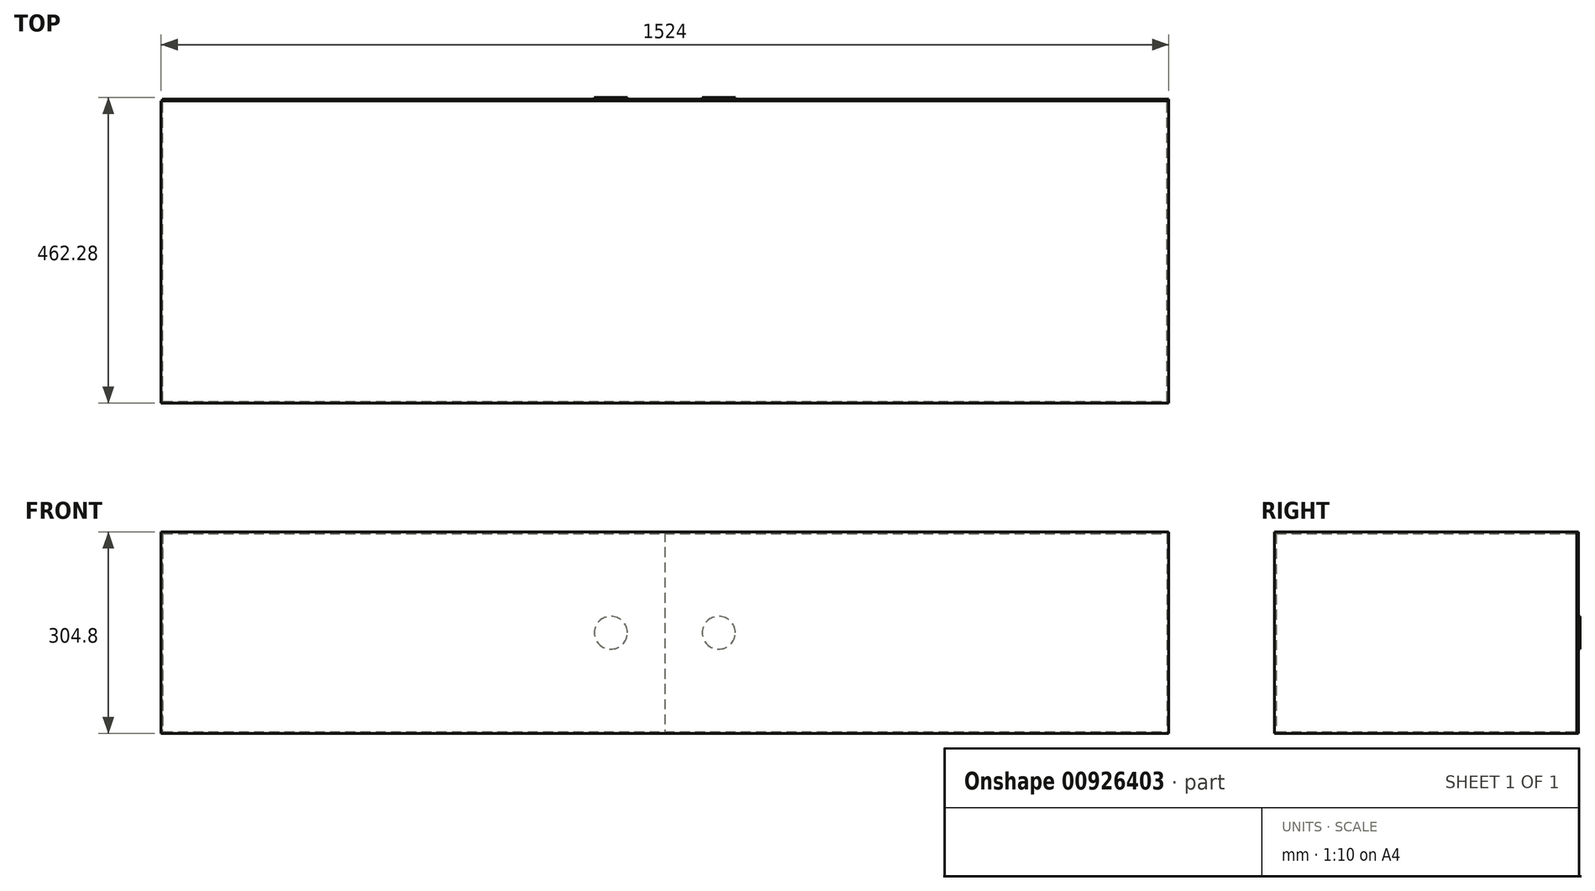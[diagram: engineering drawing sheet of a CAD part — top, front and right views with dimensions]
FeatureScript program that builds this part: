
annotation { "Feature Type Name" : "Feature", "Feature Type Description" : "" }
export const myFeature = defineFeature(function(context is Context, id is Id, definition is map)
    precondition{}
    {
        {
            var Q0;
            Q0=qCreatedBy(makeId("Front.planeOp"),FACE);
            var sketch = newSketch(context, id + "F0", { "sketchPlane" : qUnion([Q0])});
            skLineSegment(sketch, "E0.bottom", {"start": v(-36.77, 304.8) * mm, "end": v(1487.23, 304.8) * mm});
            skLineSegment(sketch, "E0.top", {"start": v(-36.77, 0) * mm, "end": v(1487.23, 0) * mm});
            skLineSegment(sketch, "E0.left", {"start": v(-36.77, 304.8) * mm, "end": v(-36.77, 0) * mm});
            skLineSegment(sketch, "E0.right", {"start": v(1487.23, 304.8) * mm, "end": v(1487.23, 0) * mm});
            skSolve(sketch);
        }
        {
            var Q0;
            Q0=makeQuery(id+"F0.imprint","IMPRINT",FACE,{"disambiguationData":[TD([[makeQuery(id+"F0.imprint","IMPRINT",EDGE,{"derivedFrom":sQuery(id+"F0.wireOp",EDGE,"E0.bottom")}),-1.0]])]});
            extrude(context, id + "F1", {"entities" : qUnion([Q0]), "depth" : 457.2 * mm, "offsetDistance" : 25.4 * mm});
        }
        {
            var Q0;
            Q0=makeQuery(id+"F1.opExtrude","CAP_FACE",FACE,{"disambiguationData":[OSD([sQuery(id+"F0.wireOp",EDGE,"E0.bottom"),sQuery(id+"F0.wireOp",EDGE,"E0.top"),sQuery(id+"F0.wireOp",EDGE,"E0.left"),sQuery(id+"F0.wireOp",EDGE,"E0.right")])],"isStart":true});
            shell(context, id + "F2", {"entities" : qUnion([Q0]), "thickness" : 2.54 * mm});
        }
        {
            var Q0;
            Q0=makeQuery(id+"F0.imprint","IMPRINT",FACE,{"disambiguationData":[TD([[makeQuery(id+"F0.imprint","IMPRINT",EDGE,{"derivedFrom":sQuery(id+"F0.wireOp",EDGE,"E0.bottom")}),-1.0]])]});
            cPlane(context, id + "F3", {"entities" : qUnion([Q0]), "cplaneType" : CPlaneType.OFFSET, "offset" : 2.54 * mm, "oppositeDirection" : true, "width" : 152.4 * mm, "height" : 152.4 * mm});
        }
        {
            var Q0;
            Q0=qCreatedBy(id+"F3.planeOp",FACE);
            var sketch = newSketch(context, id + "F4", { "sketchPlane" : qUnion([Q0])});
            skLineSegment(sketch, "E1", {"start": v(-35.28, 0) * mm, "end": v(726.72, 0) * mm, "construction": true});
            skLineSegment(sketch, "E2", {"start": v(726.72, 0) * mm, "end": v(724.98, 304.8) * mm, "construction": true});
            skLineSegment(sketch, "E3.bottom", {"start": v(724.98, 304.8) * mm, "end": v(-35.28, 304.8) * mm});
            skLineSegment(sketch, "E3.top", {"start": v(724.98, 0) * mm, "end": v(-35.28, 0) * mm});
            skLineSegment(sketch, "E3.left", {"start": v(724.98, 304.8) * mm, "end": v(724.98, 0) * mm});
            skLineSegment(sketch, "E3.right", {"start": v(-35.28, 304.8) * mm, "end": v(-35.28, 0) * mm});
            skSolve(sketch);
        }
        {
            var Q0;
            Q0 = qSketchRegion(id + "F4", true);
            extrude(context, id + "F5", {"entities" : qUnion([Q0]), "depth" : 2.54 * mm, "offsetDistance" : 25.4 * mm});
        }
        {
            var Q0;
            Q0=qCreatedBy(id+"F3.planeOp",FACE);
            var sketch = newSketch(context, id + "F6", { "sketchPlane" : qUnion([Q0])});
            skCircle(sketch, "E4.MirrorC", {"center": v(806.5, 152.4) * mm, "radius": 24.92 * mm});
            skLineSegment(sketch, "E5", {"start": v(892.15, 0) * mm, "end": v(892.15, 304.8) * mm, "construction": true});
            skLineSegment(sketch, "E6", {"start": v(806.5, 152.4) * mm, "end": v(892.15, 152.4) * mm, "construction": true});
            skLineSegment(sketch, "E7", {"start": v(724.9, 0) * mm, "end": v(724.9, 306.17) * mm, "construction": true});
            skCircle(sketch, "E8.MirrorC", {"center": v(643.31, 152.4) * mm, "radius": 24.92 * mm});
            skSolve(sketch);
        }
        {
            var Q0;
            Q0 = qSketchRegion(id + "F6", true);
            extrude(context, id + "F7", {"entities" : qUnion([Q0]), "operationType" : NewBodyOperationType.ADD, "oppositeDirection" : true, "depth" : 2.54 * mm, "offsetDistance" : 25.4 * mm});
        }
        {
            var Q0;
            Q0=qCreatedBy(id+"F3.planeOp",FACE);
            var sketch = newSketch(context, id + "F8", { "sketchPlane" : qUnion([Q0])});
            skLineSegment(sketch, "E9.bottom", {"start": v(724.98, 304.8) * mm, "end": v(1487.23, 304.8) * mm});
            skLineSegment(sketch, "E9.top", {"start": v(724.98, 0) * mm, "end": v(1487.23, 0) * mm});
            skLineSegment(sketch, "E9.left", {"start": v(724.98, 304.8) * mm, "end": v(724.98, 0) * mm});
            skLineSegment(sketch, "E9.right", {"start": v(1487.23, 304.8) * mm, "end": v(1487.23, 0) * mm});
            skSolve(sketch);
        }
        {
            var Q0;
            Q0 = qSketchRegion(id + "F8", true);
            extrude(context, id + "F9", {"entities" : qUnion([Q0]), "depth" : 2.54 * mm, "offsetDistance" : 25.4 * mm});
        }
    });
